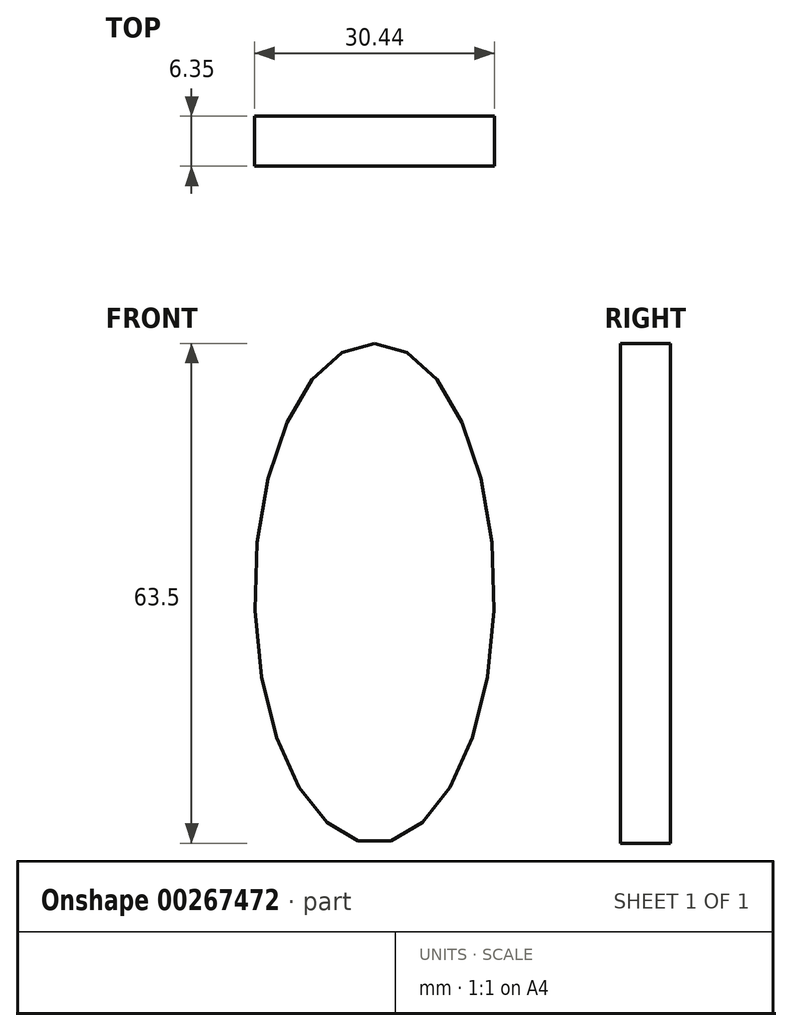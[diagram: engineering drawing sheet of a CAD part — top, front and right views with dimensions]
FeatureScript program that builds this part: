
annotation { "Feature Type Name" : "Feature", "Feature Type Description" : "" }
export const myFeature = defineFeature(function(context is Context, id is Id, definition is map)
    precondition{}
    {
        {
            var Q0;
            Q0=qCreatedBy(makeId("Front.planeOp"),FACE);
            var sketch = newSketch(context, id + "F0", { "sketchPlane" : qUnion([Q0])});
            skEllipse(sketch, "E0", {"center": v(0, 0) * mm, "majorRadius": 31.75 * mm, "minorRadius": 15.22 * mm, "majorAxis": v(0, 1)});
            skLineSegment(sketch, "E1.bottom", {"start": v(-8.68, 36.45) * mm, "end": v(8.76, 36.45) * mm});
            skLineSegment(sketch, "E1.top", {"start": v(-8.68, 25.96) * mm, "end": v(8.76, 25.96) * mm});
            skLineSegment(sketch, "E1.left", {"start": v(-8.68, 36.45) * mm, "end": v(-8.68, 25.96) * mm});
            skLineSegment(sketch, "E1.right", {"start": v(8.76, 36.45) * mm, "end": v(8.76, 25.96) * mm});
            skSolve(sketch);
        }
        {
            var Q0;
            Q0=makeQuery(id+"F0.imprint","IMPRINT",FACE,{"disambiguationData":[TD([[makeQuery(id+"F0.imprint","IMPRINT",EDGE,{"derivedFrom":sQuery(id+"F0.wireOp",EDGE,"E0")}),1.0]])]});
            extrude(context, id + "F1", {"entities" : qUnion([Q0]), "depth" : 6.35 * mm});
        }
    });
